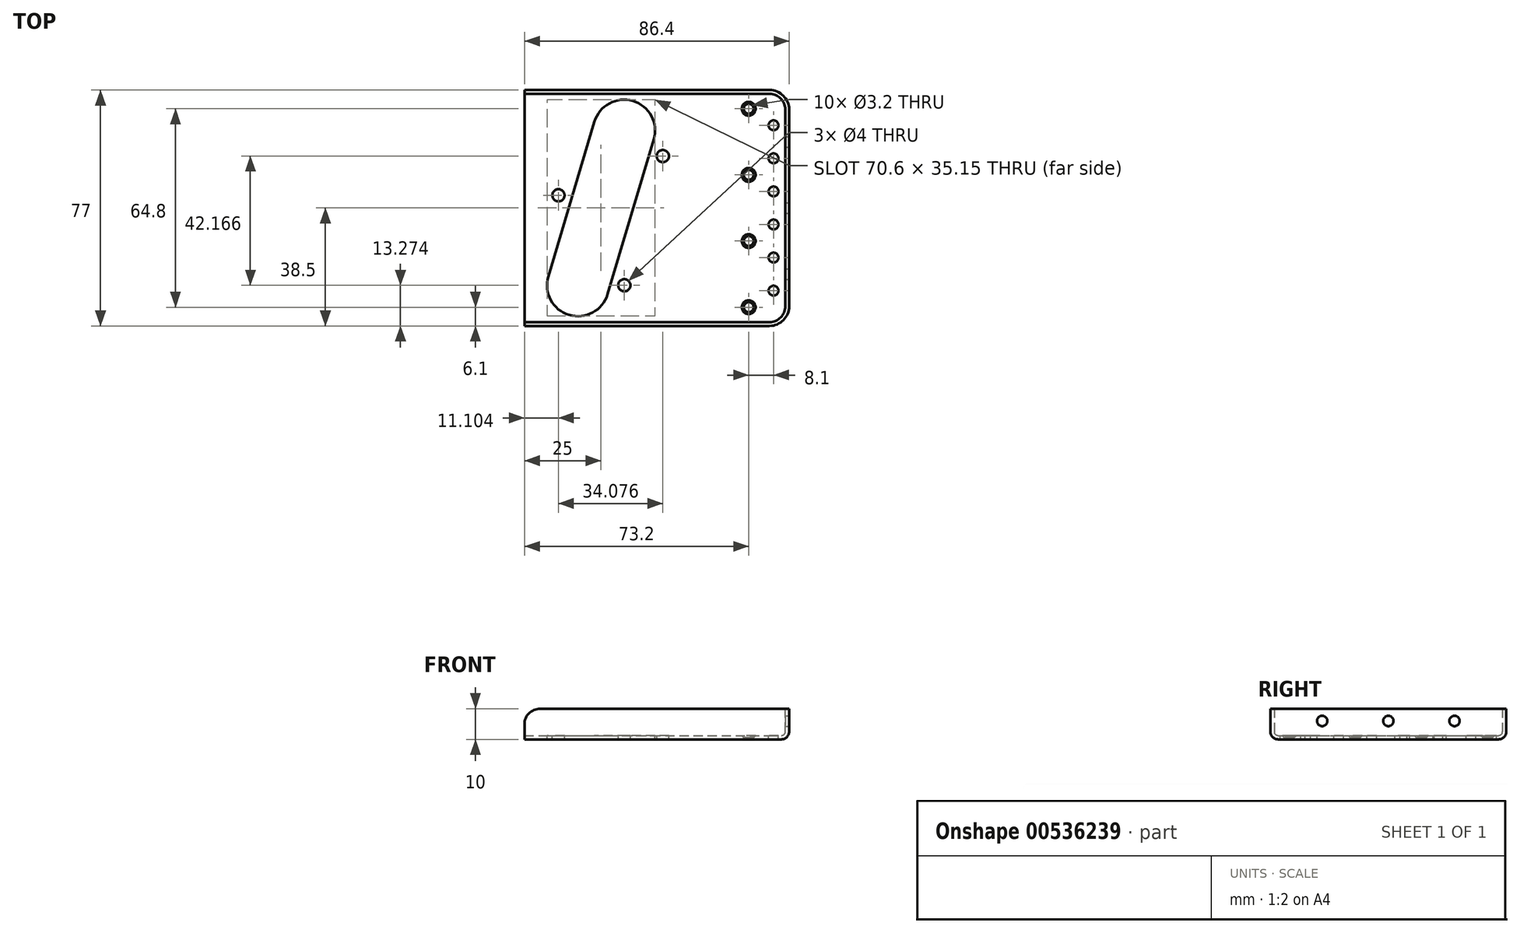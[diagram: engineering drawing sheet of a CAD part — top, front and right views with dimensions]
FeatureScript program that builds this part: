
annotation { "Feature Type Name" : "Feature", "Feature Type Description" : "" }
export const myFeature = defineFeature(function(context is Context, id is Id, definition is map)
    precondition{}
    {
        {
            var Q0;
            Q0=qCreatedBy(makeId("Top.planeOp"),FACE);
            var sketch = newSketch(context, id + "F0", { "sketchPlane" : qUnion([Q0])});
            skLineSegment(sketch, "E0.bottom", {"start": v(0, -38.5) * mm, "end": v(-86.4, -38.5) * mm});
            skLineSegment(sketch, "E0.top", {"start": v(0, 38.5) * mm, "end": v(-86.4, 38.5) * mm});
            skLineSegment(sketch, "E0.left", {"start": v(0, -38.5) * mm, "end": v(0, 38.5) * mm});
            skLineSegment(sketch, "E0.right", {"start": v(-86.4, -38.5) * mm, "end": v(-86.4, 38.5) * mm});
            skPoint(sketch, "E0.middle", {"position": v(-43.2, 0) * mm});
            skSolve(sketch);
        }
        {
            var Q0;
            Q0=qSketchRegion(id+"F0",true);
            extrude(context, id + "F1", {"entities" : qUnion([Q0]), "depth" : 10 * mm, "offsetDistance" : 25 * mm});
        }
        {
            var Q0;
            Q0=makeQuery(id+"F1.opExtrude","SWEPT_EDGE",EDGE,{"disambiguationData":[OSD([sQuery(id+"F0.wireOp",EDGE,"E0.top"),sQuery(id+"F0.wireOp",EDGE,"E0.left")])]});
            var Q1;
            Q1=makeQuery(id+"F1.opExtrude","SWEPT_EDGE",EDGE,{"disambiguationData":[OSD([sQuery(id+"F0.wireOp",EDGE,"E0.bottom"),sQuery(id+"F0.wireOp",EDGE,"E0.left")])]});
            fillet(context, id + "F2", {"entities" : qUnion([Q0, Q1]), "radius" : 6.4 * mm, "tangentPropagation" : true, "allowEdgeOverflow" : false});
        }
        {
            var Q0;
            Q0=makeQuery(id+"F1.opExtrude","CAP_EDGE",EDGE,{"disambiguationData":[OSD([sQuery(id+"F0.wireOp",EDGE,"E0.right")])],"isStart":false});
            fillet(context, id + "F3", {"entities" : qUnion([Q0]), "radius" : 5.1 * mm, "tangentPropagation" : true, "allowEdgeOverflow" : false});
        }
        {
            var Q0;
            Q0=makeQuery(id+"F1.opExtrude","CAP_EDGE",EDGE,{"disambiguationData":[OSD([sQuery(id+"F0.wireOp",EDGE,"E0.bottom")])],"isStart":true});
            fillet(context, id + "F4", {"entities" : qUnion([Q0]), "radius" : 2.5 * mm, "tangentPropagation" : true, "allowEdgeOverflow" : false});
        }
        {
            var Q0;
            Q0=makeQuery(id+"F1.opExtrude","SWEPT_FACE",FACE,{"disambiguationData":[OSD([sQuery(id+"F0.wireOp",EDGE,"E0.right")])]});
            var Q1;
            Q1=makeQuery(id+"F3.opFillet","BLEND_FACE",FACE,{"disambiguationData":[OSD([sQuery(id+"F0.wireOp",EDGE,"E0.right")])]});
            var Q2;
            Q2=makeQuery(id+"F1.opExtrude","CAP_FACE",FACE,{"disambiguationData":[OSD([sQuery(id+"F0.wireOp",EDGE,"E0.bottom"),sQuery(id+"F0.wireOp",EDGE,"E0.top"),sQuery(id+"F0.wireOp",EDGE,"E0.left"),sQuery(id+"F0.wireOp",EDGE,"E0.right")])],"isStart":false});
            shell(context, id + "F5", {"entities" : qUnion([Q0, Q1, Q2]), "thickness" : 1.25 * mm});
        }
        {
            var Q0;
            {var subQ0=sQuery(id+"F0.wireOp",EDGE,"E0.right");var subQ1=sQuery(id+"F0.wireOp",EDGE,"E0.left");var subQ2=sQuery(id+"F0.wireOp",EDGE,"E0.top");var subQ3=sQuery(id+"F0.wireOp",EDGE,"E0.bottom");Q0=makeQuery(id+"F5.opShell","OFFSET_FACE",FACE,{"disambiguationData":[OSD([subQ3,subQ2,subQ1,subQ0]),TDD([makeQuery(id+"F1.opExtrude","CAP_FACE",FACE,{"disambiguationData":[OSD([subQ3,subQ2,subQ1,subQ0])],"isStart":true})])]});}
            var sketch = newSketch(context, id + "F6", { "sketchPlane" : qUnion([Q0])});
            skLineSegment(sketch, "E1", {"start": v(-68.93, -25.25) * mm, "end": v(-53.87, 25.25) * mm, "construction": true});
            skArc(sketch, "E2.0.startCap", {"start": v(-59.25, -28.14) * mm, "mid": v(-71.81, -34.93) * mm, "end": v(-78.6, -22.37) * mm});
            skArc(sketch, "E2.0.endCap", {"start": v(-63.55, 28.14) * mm, "mid": v(-50.99, 34.93) * mm, "end": v(-44.2, 22.37) * mm});
            skLineSegment(sketch, "E2.0.left", {"start": v(-78.6, -22.37) * mm, "end": v(-63.55, 28.14) * mm});
            skLineSegment(sketch, "E2.0.right", {"start": v(-59.25, -28.14) * mm, "end": v(-44.2, 22.37) * mm});
            skPoint(sketch, "E3", {"position": v(-61.4, 0) * mm});
            skLineSegment(sketch, "E4", {"start": v(0, 0) * mm, "end": v(-86.4, 0) * mm, "construction": true});
            skSolve(sketch);
        }
        {
            var Q0;
            Q0=qSketchRegion(id+"F6",true);
            extrude(context, id + "F7", {"entities" : qUnion([Q0]), "operationType" : NewBodyOperationType.REMOVE, "endBound" : BoundingType.THROUGH_ALL, "oppositeDirection" : true, "depth" : 25 * mm, "offsetDistance" : 25 * mm});
        }
        {
            var Q0;
            Q0=makeQuery(id+"F6.imprint","IMPRINT",FACE,{"disambiguationData":[TD([[makeQuery(id+"F6.imprint","IMPRINT",EDGE,{"derivedFrom":sQuery(id+"F6.wireOp",EDGE,"E2.0.startCap")}),1.0]])]});
            var sketch = newSketch(context, id + "F8", { "sketchPlane" : qUnion([Q0])});
            skLineSegment(sketch, "E5", {"start": v(-75.3, 4.14) * mm, "end": v(-47.5, -4.14) * mm, "construction": true});
            skLineSegment(sketch, "E6", {"start": v(-41.22, 16.94) * mm, "end": v(-53.79, -25.23) * mm, "construction": true});
            skSolve(sketch);
        }
        {
            var Q0;
            Q0=sQuery(id+"F8.wireOp",VERTEX,"E5.start");
            var Q1;
            Q1=sQuery(id+"F8.wireOp",VERTEX,"E6.start");
            var Q2;
            Q2=sQuery(id+"F8.wireOp",VERTEX,"E6.end");
            var Q3;
            Q3=makeQuery(id+"F1.opExtrude","SWEPT_BODY",BODY,{"disambiguationData":[OSD([sQuery(id+"F0.wireOp",EDGE,"E0.bottom"),sQuery(id+"F0.wireOp",EDGE,"E0.top"),sQuery(id+"F0.wireOp",EDGE,"E0.left"),sQuery(id+"F0.wireOp",EDGE,"E0.right")])]});
            hole(context, id + "F9", {"style" : HoleStyle.SIMPLE, "endStyle" : HoleEndStyle.THROUGH, "standardTappedOrClearance" : lookupTablePath({ "standard" : "ISO", "size" : "4", "type" : "Drilled" }), "standardBlindInLast" : lookupTablePath({ "standard" : "ISO", "size" : "4", "type" : "Drilled" }), "holeDiameter" : 4 * mm, "isTappedThrough" : true, "tappedDepth" : 12 * mm, "tapClearance" : 3, "locations" : qUnion([Q0, Q1, Q2]), "scope" : qUnion([Q3])});
        }
        {
            var Q0;
            {var subQ0=sQuery(id+"F0.wireOp",EDGE,"E0.right");var subQ1=sQuery(id+"F0.wireOp",EDGE,"E0.left");var subQ2=sQuery(id+"F0.wireOp",EDGE,"E0.top");var subQ3=sQuery(id+"F0.wireOp",EDGE,"E0.bottom");Q0=makeQuery(id+"F5.opShell","OFFSET_FACE",FACE,{"disambiguationData":[OSD([subQ3,subQ2,subQ1,subQ0]),TDD([makeQuery(id+"F1.opExtrude","CAP_FACE",FACE,{"disambiguationData":[OSD([subQ3,subQ2,subQ1,subQ0])],"isStart":true})])]});}
            var sketch = newSketch(context, id + "F10", { "sketchPlane" : qUnion([Q0])});
            skLineSegment(sketch, "E7", {"start": v(0, 0) * mm, "end": v(-105.76, 0) * mm, "construction": true});
            skLineSegment(sketch, "E8", {"start": v(-5.1, 27) * mm, "end": v(-5.1, -27) * mm, "construction": true});
            skPoint(sketch, "E9", {"position": v(-5.1, -5.4) * mm});
            skPoint(sketch, "E10", {"position": v(-5.1, -16.2) * mm});
            skPoint(sketch, "E11", {"position": v(-5.1, 5.4) * mm});
            skPoint(sketch, "E12", {"position": v(-5.1, 16.2) * mm});
            skSolve(sketch);
        }
        {
            var Q0;
            Q0=sQuery(id+"F10.wireOp",VERTEX,"E8.end");
            var Q1;
            Q1=sQuery(id+"F10.wireOp",VERTEX,"E10");
            var Q2;
            Q2=sQuery(id+"F10.wireOp",VERTEX,"E9");
            var Q3;
            Q3=sQuery(id+"F10.wireOp",VERTEX,"E11");
            var Q4;
            Q4=sQuery(id+"F10.wireOp",VERTEX,"E12");
            var Q5;
            Q5=sQuery(id+"F10.wireOp",VERTEX,"E8.start");
            var Q6;
            Q6=makeQuery(id+"F1.opExtrude","SWEPT_BODY",BODY,{"disambiguationData":[OSD([sQuery(id+"F0.wireOp",EDGE,"E0.bottom"),sQuery(id+"F0.wireOp",EDGE,"E0.top"),sQuery(id+"F0.wireOp",EDGE,"E0.left"),sQuery(id+"F0.wireOp",EDGE,"E0.right")])]});
            hole(context, id + "F11", {"style" : HoleStyle.SIMPLE, "endStyle" : HoleEndStyle.THROUGH, "standardTappedOrClearance" : lookupTablePath({ "standard" : "ISO", "size" : "3.2", "type" : "Drilled" }), "standardBlindInLast" : lookupTablePath({ "standard" : "ISO", "size" : "3.2", "type" : "Drilled" }), "holeDiameter" : 3.2 * mm, "isTappedThrough" : true, "tappedDepth" : 12 * mm, "tapClearance" : 3, "locations" : qUnion([Q0, Q1, Q2, Q3, Q4, Q5]), "scope" : qUnion([Q6])});
        }
        {
            var Q0;
            Q0=makeQuery(id+"F1.opExtrude","SWEPT_FACE",FACE,{"disambiguationData":[OSD([sQuery(id+"F0.wireOp",EDGE,"E0.left")])]});
            var sketch = newSketch(context, id + "F12", { "sketchPlane" : qUnion([Q0])});
            skLineSegment(sketch, "E13", {"start": v(-21.6, 6) * mm, "end": v(21.6, 6) * mm, "construction": true});
            skLineSegment(sketch, "E14", {"start": v(0, 0) * mm, "end": v(0, 10) * mm, "construction": true});
            skPoint(sketch, "E15", {"position": v(0, 6) * mm});
            skSolve(sketch);
        }
        {
            var Q0;
            Q0=sQuery(id+"F12.wireOp",VERTEX,"E13.start");
            var Q1;
            Q1=sQuery(id+"F12.wireOp",VERTEX,"E15");
            var Q2;
            Q2=sQuery(id+"F12.wireOp",VERTEX,"E13.end");
            var Q3;
            Q3=makeQuery(id+"F1.opExtrude","SWEPT_BODY",BODY,{"disambiguationData":[OSD([sQuery(id+"F0.wireOp",EDGE,"E0.bottom"),sQuery(id+"F0.wireOp",EDGE,"E0.top"),sQuery(id+"F0.wireOp",EDGE,"E0.left"),sQuery(id+"F0.wireOp",EDGE,"E0.right")])]});
            hole(context, id + "F13", {"style" : HoleStyle.SIMPLE, "endStyle" : HoleEndStyle.THROUGH, "standardTappedOrClearance" : lookupTablePath({ "standard" : "ISO", "size" : "3.4", "type" : "Drilled" }), "standardBlindInLast" : lookupTablePath({ "standard" : "ISO", "size" : "3.4", "type" : "Drilled" }), "holeDiameter" : 3.4 * mm, "isTappedThrough" : true, "tappedDepth" : 12 * mm, "tapClearance" : 3, "locations" : qUnion([Q0, Q1, Q2]), "scope" : qUnion([Q3])});
        }
        {
            var Q0;
            {var subQ0=sQuery(id+"F0.wireOp",EDGE,"E0.right");var subQ1=sQuery(id+"F0.wireOp",EDGE,"E0.left");var subQ2=sQuery(id+"F0.wireOp",EDGE,"E0.top");var subQ3=sQuery(id+"F0.wireOp",EDGE,"E0.bottom");Q0=makeQuery(id+"F5.opShell","OFFSET_FACE",FACE,{"disambiguationData":[OSD([subQ3,subQ2,subQ1,subQ0]),TDD([makeQuery(id+"F1.opExtrude","CAP_FACE",FACE,{"disambiguationData":[OSD([subQ3,subQ2,subQ1,subQ0])],"isStart":true})])]});}
            var sketch = newSketch(context, id + "F14", { "sketchPlane" : qUnion([Q0])});
            skLineSegment(sketch, "E16", {"start": v(-13.2, 32.4) * mm, "end": v(-13.2, -32.4) * mm, "construction": true});
            skLineSegment(sketch, "E17", {"start": v(0, 0) * mm, "end": v(-13.2, 0) * mm, "construction": true});
            skPoint(sketch, "E18", {"position": v(-5.1, -27) * mm});
            skPoint(sketch, "E19", {"position": v(-13.2, 10.8) * mm});
            skPoint(sketch, "E20", {"position": v(-13.2, -10.8) * mm});
            skSolve(sketch);
        }
        {
            var Q0;
            Q0=sQuery(id+"F14.wireOp",VERTEX,"E16.end");
            var Q1;
            Q1=sQuery(id+"F14.wireOp",VERTEX,"E20");
            var Q2;
            Q2=sQuery(id+"F14.wireOp",VERTEX,"E19");
            var Q3;
            Q3=sQuery(id+"F14.wireOp",VERTEX,"E16.start");
            var Q4;
            Q4=makeQuery(id+"F1.opExtrude","SWEPT_BODY",BODY,{"disambiguationData":[OSD([sQuery(id+"F0.wireOp",EDGE,"E0.bottom"),sQuery(id+"F0.wireOp",EDGE,"E0.top"),sQuery(id+"F0.wireOp",EDGE,"E0.left"),sQuery(id+"F0.wireOp",EDGE,"E0.right")])]});
            hole(context, id + "F15", {"style" : HoleStyle.C_SINK, "endStyle" : HoleEndStyle.THROUGH, "standardTappedOrClearance" : lookupTablePath({ "standard" : "ISO", "size" : "3.2", "type" : "Drilled" }), "standardBlindInLast" : lookupTablePath({ "standard" : "ISO", "size" : "3.2", "type" : "Drilled" }), "holeDiameter" : 3.2 * mm, "cSinkDiameter" : 4.5 * mm, "cSinkAngle" : 90 * degree, "isTappedThrough" : true, "tappedDepth" : 12 * mm, "tapClearance" : 3, "locations" : qUnion([Q0, Q1, Q2, Q3]), "scope" : qUnion([Q4])});
        }
    });
